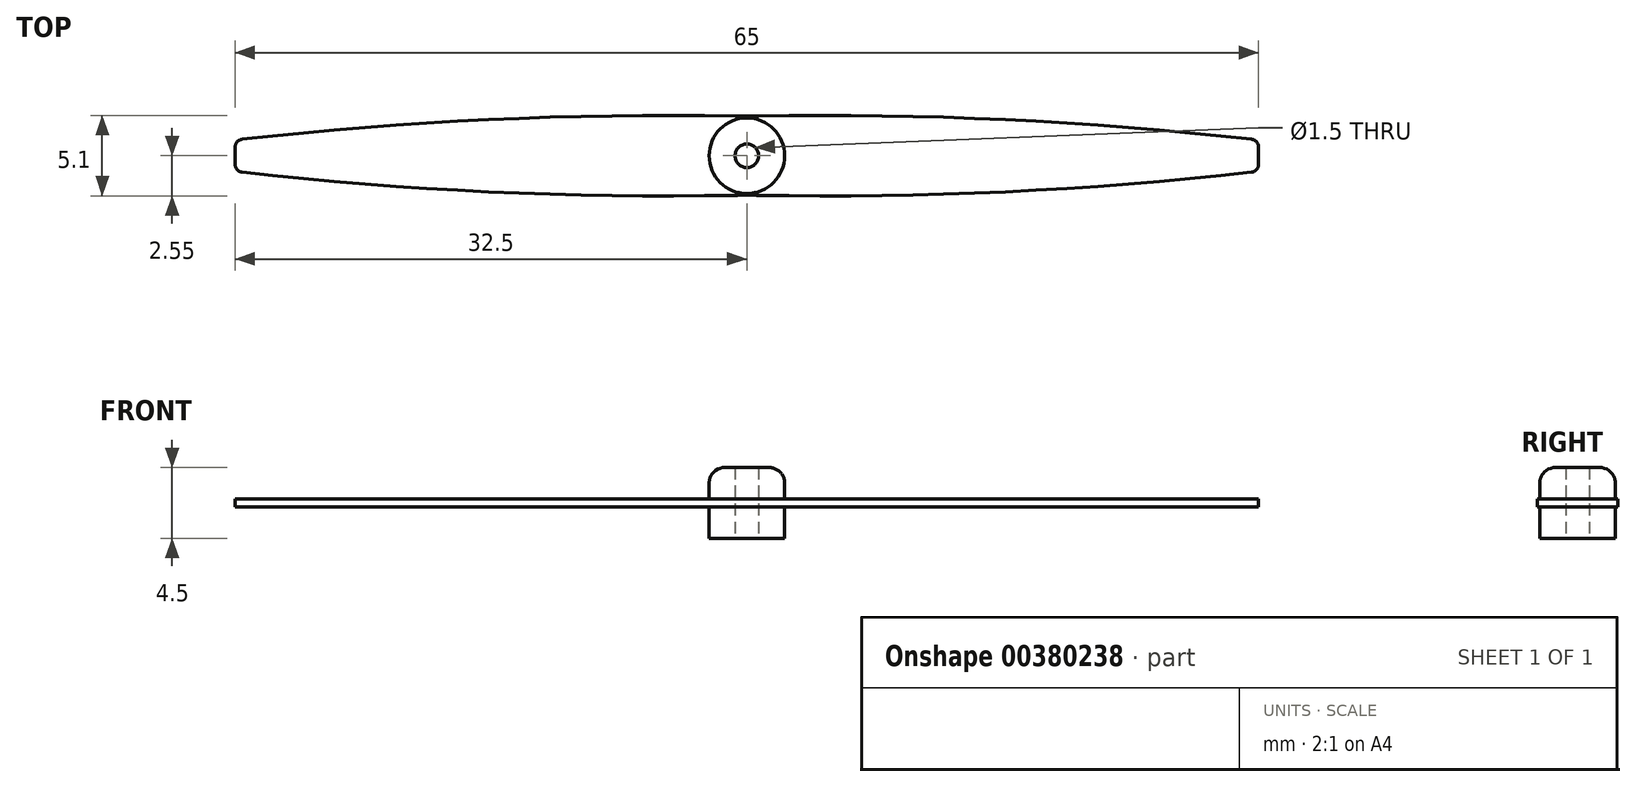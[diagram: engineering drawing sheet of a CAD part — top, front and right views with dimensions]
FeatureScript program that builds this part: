
annotation { "Feature Type Name" : "Feature", "Feature Type Description" : "" }
export const myFeature = defineFeature(function(context is Context, id is Id, definition is map)
    precondition{}
    {
        {
            var Q0;
            Q0=qCreatedBy(makeId("Top.planeOp"),FACE);
            var sketch = newSketch(context, id + "F0", { "sketchPlane" : qUnion([Q0])});
            skCircle(sketch, "E0", {"center": v(0, 0) * mm, "radius": 0.75 * mm});
            skLineSegment(sketch, "E1", {"start": v(0, 0) * mm, "end": v(32.5, 0) * mm, "construction": true});
            skLineSegment(sketch, "E2", {"start": v(-32.5, 0.55) * mm, "end": v(-32.5, -0.55) * mm});
            skArc(sketch, "E3", {"start": v(-0.73, 2.51) * mm, "mid": v(-16.42, 2.3) * mm, "end": v(-32.06, 1.05) * mm});
            skArc(sketch, "E4.MirrorCS", {"start": v(-0.73, -2.51) * mm, "mid": v(-16.42, -2.3) * mm, "end": v(-32.06, -1.05) * mm});
            skLineSegment(sketch, "E5", {"start": v(0, 0) * mm, "end": v(0, -1.98) * mm, "construction": true});
            skArc(sketch, "E6.MirrorCS", {"start": v(0.73, -2.51) * mm, "mid": v(16.42, -2.3) * mm, "end": v(32.06, -1.05) * mm});
            skArc(sketch, "E7.MirrorCS", {"start": v(0.73, 2.51) * mm, "mid": v(16.42, 2.3) * mm, "end": v(32.06, 1.05) * mm});
            skLineSegment(sketch, "E8.MirrorCS", {"start": v(32.5, 0.55) * mm, "end": v(32.5, -0.55) * mm});
            skPoint(sketch, "E9.visualSharp", {"position": v(-32.5, 1) * mm});
            skArc(sketch, "E9.filletArc", {"start": v(-32.06, 1.05) * mm, "mid": v(-32.37, 0.89) * mm, "end": v(-32.5, 0.55) * mm});
            skPoint(sketch, "E10.visualSharp", {"position": v(-32.5, -1) * mm});
            skArc(sketch, "E10.filletArc", {"start": v(-32.5, -0.55) * mm, "mid": v(-32.37, -0.89) * mm, "end": v(-32.06, -1.05) * mm});
            skPoint(sketch, "E11.visualSharp", {"position": v(32.5, 1) * mm});
            skArc(sketch, "E11.filletArc", {"start": v(32.5, 0.55) * mm, "mid": v(32.37, 0.89) * mm, "end": v(32.06, 1.05) * mm});
            skPoint(sketch, "E12.visualSharp", {"position": v(32.5, -1) * mm});
            skArc(sketch, "E12.filletArc", {"start": v(32.06, -1.05) * mm, "mid": v(32.37, -0.89) * mm, "end": v(32.5, -0.55) * mm});
            skPoint(sketch, "E13.visualSharp", {"position": v(0, 2.5) * mm});
            skArc(sketch, "E13.filletArc", {"start": v(-0.73, 2.51) * mm, "mid": v(0, 2.5) * mm, "end": v(0.73, 2.51) * mm});
            skPoint(sketch, "E14.visualSharp", {"position": v(0, -2.5) * mm});
            skArc(sketch, "E14.filletArc", {"start": v(0.73, -2.51) * mm, "mid": v(0, -2.5) * mm, "end": v(-0.73, -2.51) * mm});
            skSolve(sketch);
        }
        {
            var Q0;
            Q0=makeQuery(id+"F0.imprint","IMPRINT",FACE,{"disambiguationData":[TD([[makeQuery(id+"F0.imprint","IMPRINT",EDGE,{"derivedFrom":sQuery(id+"F0.wireOp",EDGE,"E0")}),-1.0]])]});
            extrude(context, id + "F1", {"entities" : qUnion([Q0]), "depth" : 0.5 * mm});
        }
        {
            var Q0;
            Q0=makeQuery(id+"F1.opExtrude","CAP_FACE",FACE,{"disambiguationData":[OSD([sQuery(id+"F0.wireOp",EDGE,"E0"),sQuery(id+"F0.wireOp",EDGE,"E2"),sQuery(id+"F0.wireOp",EDGE,"E3"),sQuery(id+"F0.wireOp",EDGE,"E4.MirrorCS"),sQuery(id+"F0.wireOp",EDGE,"E6.MirrorCS"),sQuery(id+"F0.wireOp",EDGE,"E7.MirrorCS"),sQuery(id+"F0.wireOp",EDGE,"E8.MirrorCS"),sQuery(id+"F0.wireOp",EDGE,"E9.filletArc"),sQuery(id+"F0.wireOp",EDGE,"E10.filletArc"),sQuery(id+"F0.wireOp",EDGE,"E11.filletArc"),sQuery(id+"F0.wireOp",EDGE,"E12.filletArc"),sQuery(id+"F0.wireOp",EDGE,"E13.filletArc"),sQuery(id+"F0.wireOp",EDGE,"E14.filletArc")])],"isStart":false});
            var sketch = newSketch(context, id + "F2", { "sketchPlane" : qUnion([Q0])});
            skCircle(sketch, "E15", {"center": v(0, 0) * mm, "radius": 2.4 * mm});
            skSolve(sketch);
        }
        {
            var Q0;
            Q0=makeQuery(id+"F2.imprint","IMPRINT",FACE,{"disambiguationData":[TD([[makeQuery(id+"F2.imprint","IMPRINT",EDGE,{"derivedFrom":sQuery(id+"F2.wireOp",EDGE,"E15")}),1.0]])]});
            extrude(context, id + "F3", {"entities" : qUnion([Q0]), "operationType" : NewBodyOperationType.ADD, "depth" : 2 * mm});
        }
        {
            var Q0;
            Q0=makeQuery(id+"F3.opExtrude","CAP_EDGE",EDGE,{"disambiguationData":[OSD([sQuery(id+"F2.wireOp",EDGE,"E15")])],"isStart":false});
            fillet(context, id + "F4", {"entities" : qUnion([Q0]), "radius" : 1 * mm, "tangentPropagation" : true, "allowEdgeOverflow" : false});
        }
        {
            var Q0;
            Q0=makeQuery(id+"F1.opExtrude","CAP_FACE",FACE,{"disambiguationData":[OSD([sQuery(id+"F0.wireOp",EDGE,"E0"),sQuery(id+"F0.wireOp",EDGE,"E2"),sQuery(id+"F0.wireOp",EDGE,"E3"),sQuery(id+"F0.wireOp",EDGE,"E4.MirrorCS"),sQuery(id+"F0.wireOp",EDGE,"E6.MirrorCS"),sQuery(id+"F0.wireOp",EDGE,"E7.MirrorCS"),sQuery(id+"F0.wireOp",EDGE,"E8.MirrorCS"),sQuery(id+"F0.wireOp",EDGE,"E9.filletArc"),sQuery(id+"F0.wireOp",EDGE,"E10.filletArc"),sQuery(id+"F0.wireOp",EDGE,"E11.filletArc"),sQuery(id+"F0.wireOp",EDGE,"E12.filletArc"),sQuery(id+"F0.wireOp",EDGE,"E13.filletArc"),sQuery(id+"F0.wireOp",EDGE,"E14.filletArc")])],"isStart":true});
            var sketch = newSketch(context, id + "F5", { "sketchPlane" : qUnion([Q0])});
            skCircle(sketch, "E16", {"center": v(0, 0) * mm, "radius": 2.4 * mm});
            skSolve(sketch);
        }
        {
            var Q0;
            Q0=makeQuery(id+"F5.imprint","IMPRINT",FACE,{"disambiguationData":[TD([[makeQuery(id+"F5.imprint","IMPRINT",EDGE,{"derivedFrom":sQuery(id+"F5.wireOp",EDGE,"E16")}),1.0]])]});
            extrude(context, id + "F6", {"entities" : qUnion([Q0]), "operationType" : NewBodyOperationType.ADD, "depth" : 2 * mm});
        }
    });
